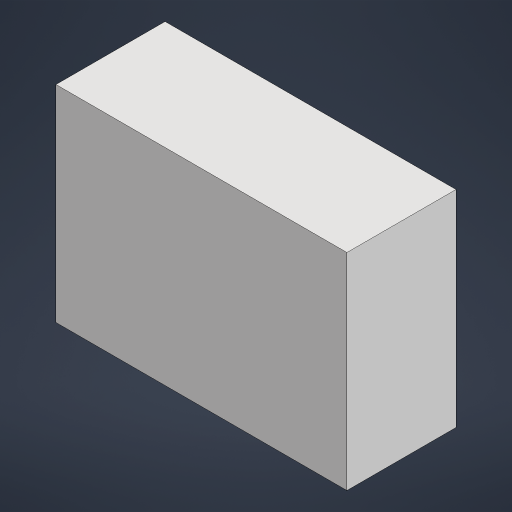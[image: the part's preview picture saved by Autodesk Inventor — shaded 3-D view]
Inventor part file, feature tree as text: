
AUTODESK INVENTOR PART (.ipt)
format: ipt  version: 2023.2 (Build 272271000, 271)  size: 131,072 bytes
history: native  units: in
note: dims shown in document units (in); Inventor stores cm internally (conversion verified against a paired STEP export)
features: extrude x1, sketch x1
ambient origin geometry x8: Origin, YZ Plane, XZ Plane, XY Plane, X Axis, Y Axis, Z Axis, Center Point
bodies: Solid1 (feature_tree)
feature tree (2):
  extrude  "Extrusion1"  Depth=18.0in
  sketch  "Sketch2"  dims[d3=48.0in d4=18.0in d5=34.0in d6=0.0in]
